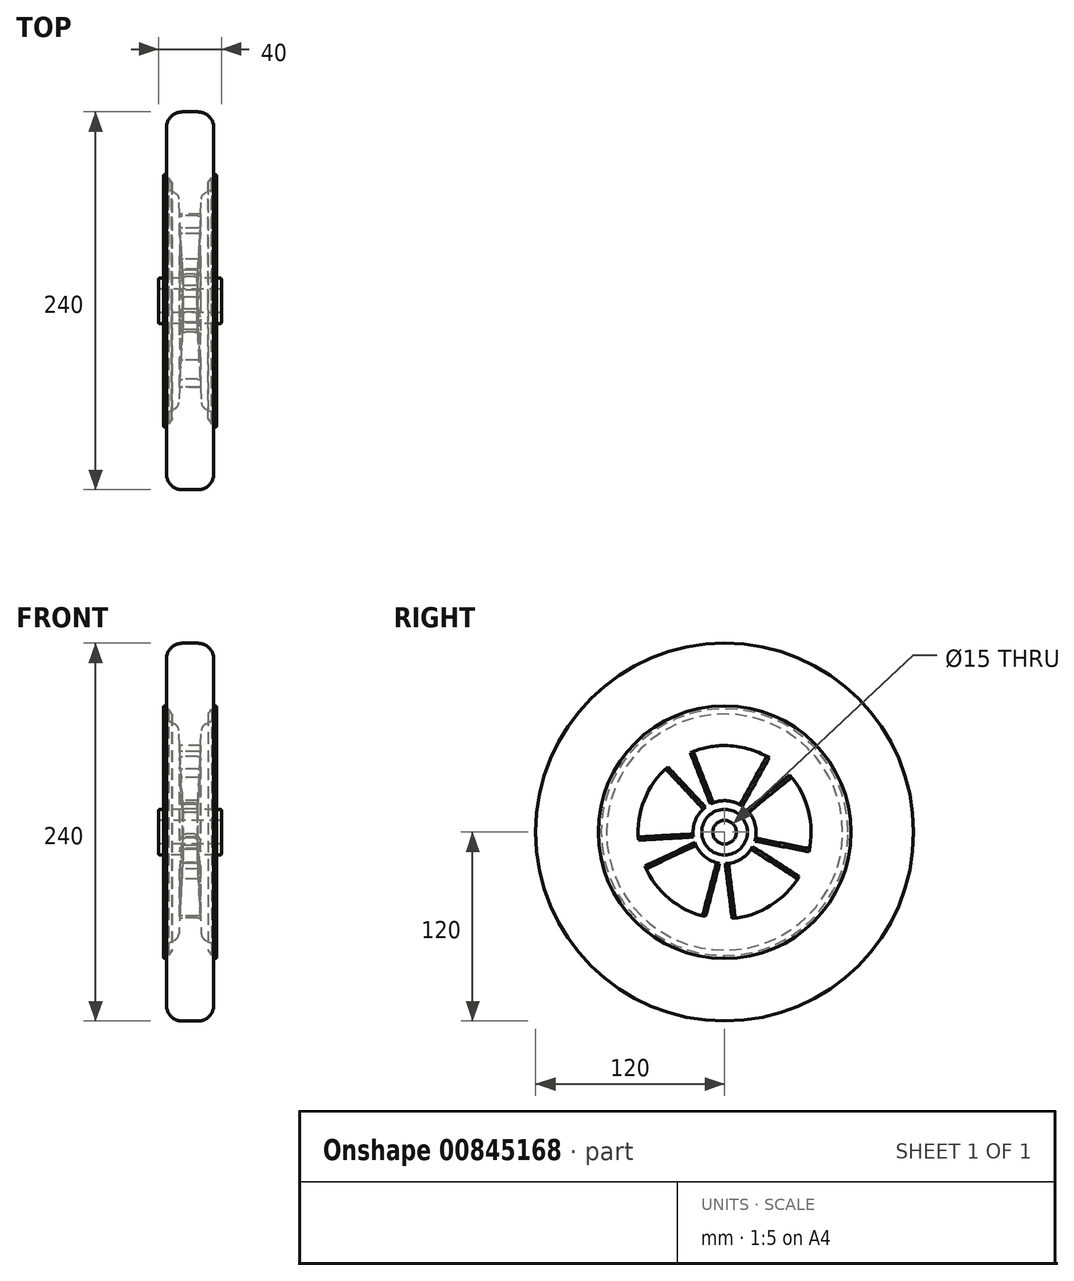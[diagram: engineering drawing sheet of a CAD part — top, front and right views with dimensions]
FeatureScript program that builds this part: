
annotation { "Feature Type Name" : "Feature", "Feature Type Description" : "" }
export const myFeature = defineFeature(function(context is Context, id is Id, definition is map)
    precondition{}
    {
        {
            var Q0;
            Q0=qCreatedBy(makeId("Top.planeOp"),FACE);
            var sketch = newSketch(context, id + "F0", { "sketchPlane" : qUnion([Q0])});
            skLineSegment(sketch, "E0", {"start": v(-229, 0) * mm, "end": v(229, 0) * mm});
            skLineSegment(sketch, "E1", {"start": v(0, 0) * mm, "end": v(0, 120) * mm, "construction": true});
            skLineSegment(sketch, "E2", {"start": v(0, 7.5) * mm, "end": v(-20, 7.5) * mm});
            skLineSegment(sketch, "E3", {"start": v(-20, 7.5) * mm, "end": v(-20, 14.5) * mm});
            skLineSegment(sketch, "E4", {"start": v(-20, 14.5) * mm, "end": v(-4.5, 14.5) * mm});
            skLineSegment(sketch, "E5", {"start": v(-4.5, 14.5) * mm, "end": v(-7.12, 64.5) * mm});
            skLineSegment(sketch, "E6", {"start": v(0, 75) * mm, "end": v(-11.6, 75) * mm});
            skLineSegment(sketch, "E7", {"start": v(-11.6, 75) * mm, "end": v(-14.88, 80.24) * mm});
            skLineSegment(sketch, "E8", {"start": v(-14.88, 80.24) * mm, "end": v(-15.88, 80.24) * mm});
            skLineSegment(sketch, "E9", {"start": v(-9.92, 68.72) * mm, "end": v(-13.12, 70.29) * mm});
            skLineSegment(sketch, "E10", {"start": v(-13.61, 70.82) * mm, "end": v(-16.8, 78.88) * mm});
            skPoint(sketch, "E11.visualSharp", {"position": v(-17.35, 80.24) * mm});
            skArc(sketch, "E11.filletArc", {"start": v(-15.88, 80.24) * mm, "mid": v(-16.7, 79.8) * mm, "end": v(-16.8, 78.88) * mm});
            skPoint(sketch, "E12.visualSharp", {"position": v(-13.47, 70.46) * mm});
            skArc(sketch, "E12.filletArc", {"start": v(-13.61, 70.82) * mm, "mid": v(-13.42, 70.5) * mm, "end": v(-13.12, 70.29) * mm});
            skPoint(sketch, "E13.visualSharp", {"position": v(-7.27, 67.43) * mm});
            skArc(sketch, "E13.filletArc", {"start": v(-7.12, 64.5) * mm, "mid": v(-7.94, 66.99) * mm, "end": v(-9.92, 68.72) * mm});
            skLineSegment(sketch, "E14", {"start": v(0, 120) * mm, "end": v(-5, 120) * mm});
            skLineSegment(sketch, "E15", {"start": v(-15, 110) * mm, "end": v(-15, 80.8) * mm});
            skLineSegment(sketch, "E16", {"start": v(-14.75, 79.97) * mm, "end": v(-11.5, 75) * mm});
            skLineSegment(sketch, "E17", {"start": v(-11.5, 75) * mm, "end": v(0, 75) * mm});
            skPoint(sketch, "E18.visualSharp", {"position": v(-15, 80.35) * mm});
            skArc(sketch, "E18.filletArc", {"start": v(-15, 80.8) * mm, "mid": v(-14.94, 80.36) * mm, "end": v(-14.75, 79.97) * mm});
            skPoint(sketch, "E19.visualSharp", {"position": v(-15, 120) * mm});
            skArc(sketch, "E19.filletArc", {"start": v(-5, 120) * mm, "mid": v(-12.07, 117.07) * mm, "end": v(-15, 110) * mm});
            skLineSegment(sketch, "E20.MirrorCS", {"start": v(0, 7.5) * mm, "end": v(20, 7.5) * mm});
            skLineSegment(sketch, "E21.MirrorCS", {"start": v(20, 7.5) * mm, "end": v(20, 14.5) * mm});
            skLineSegment(sketch, "E22.MirrorCS", {"start": v(20, 14.5) * mm, "end": v(4.5, 14.5) * mm});
            skLineSegment(sketch, "E23.MirrorCS", {"start": v(4.5, 14.5) * mm, "end": v(7.12, 64.5) * mm});
            skArc(sketch, "E24.MirrorCS", {"start": v(7.12, 64.5) * mm, "mid": v(7.94, 66.99) * mm, "end": v(9.92, 68.72) * mm});
            skLineSegment(sketch, "E25.MirrorCS", {"start": v(9.92, 68.72) * mm, "end": v(13.12, 70.29) * mm});
            skArc(sketch, "E26.MirrorCS", {"start": v(13.61, 70.82) * mm, "mid": v(13.42, 70.5) * mm, "end": v(13.12, 70.29) * mm});
            skLineSegment(sketch, "E27.MirrorCS", {"start": v(13.61, 70.82) * mm, "end": v(16.8, 78.88) * mm});
            skArc(sketch, "E28.MirrorCS", {"start": v(15.88, 80.24) * mm, "mid": v(16.7, 79.8) * mm, "end": v(16.8, 78.88) * mm});
            skLineSegment(sketch, "E29.MirrorCS", {"start": v(14.88, 80.24) * mm, "end": v(15.88, 80.24) * mm});
            skLineSegment(sketch, "E30.MirrorCS", {"start": v(11.6, 75) * mm, "end": v(14.88, 80.24) * mm});
            skLineSegment(sketch, "E31.MirrorCS", {"start": v(0, 75) * mm, "end": v(11.6, 75) * mm});
            skLineSegment(sketch, "E32.MirrorCS", {"start": v(11.5, 75) * mm, "end": v(0, 75) * mm});
            skLineSegment(sketch, "E33.MirrorCS", {"start": v(14.75, 79.97) * mm, "end": v(11.5, 75) * mm});
            skArc(sketch, "E34.MirrorCS", {"start": v(15, 80.8) * mm, "mid": v(14.94, 80.36) * mm, "end": v(14.75, 79.97) * mm});
            skLineSegment(sketch, "E35.MirrorCS", {"start": v(15, 110) * mm, "end": v(15, 80.8) * mm});
            skArc(sketch, "E36.MirrorCS", {"start": v(5, 120) * mm, "mid": v(12.07, 117.07) * mm, "end": v(15, 110) * mm});
            skLineSegment(sketch, "E37.MirrorCS", {"start": v(0, 120) * mm, "end": v(5, 120) * mm});
            skSolve(sketch);
        }
        {
            var Q0;
            {var subQ0=sQuery(id+"F0.wireOp",EDGE,"E8");var subQ1=sQuery(id+"F0.wireOp",EDGE,"E7");var subQ2=makeQuery(id+"F0.imprint","INTERSECT",VERTEX,{"derivedFrom":[subQ1,subQ0]});Q0=makeQuery(id+"F0.imprint","IMPRINT",FACE,{"disambiguationData":[TD([[makeQuery(id+"F0.imprint","IMPRINT",EDGE,{"disambiguationData":[TD([[subQ2,1.0]])],"derivedFrom":subQ1}),1.0]])]});}
            var Q1;
            {var subQ0=sQuery(id+"F0.wireOp",EDGE,"E30.MirrorCS");var subQ1=sQuery(id+"F0.wireOp",EDGE,"E29.MirrorCS");var subQ2=makeQuery(id+"F0.imprint","INTERSECT",VERTEX,{"derivedFrom":[subQ1,subQ0]});Q1=makeQuery(id+"F0.imprint","IMPRINT",FACE,{"disambiguationData":[TD([[makeQuery(id+"F0.imprint","IMPRINT",EDGE,{"disambiguationData":[TD([[subQ2,-1.0]])],"derivedFrom":subQ1}),-1.0]])]});}
            var Q2;
            Q2=makeQuery(id+"F0.imprint","IMPRINT",FACE,{"disambiguationData":[TD([[makeQuery(id+"F0.imprint","IMPRINT",EDGE,{"derivedFrom":sQuery(id+"F0.wireOp",EDGE,"E14")}),1.0]])]});
            var Q3;
            Q3=makeQuery(id+"F0.imprint","IMPRINT",FACE,{"disambiguationData":[TD([[makeQuery(id+"F0.imprint","IMPRINT",EDGE,{"derivedFrom":sQuery(id+"F0.wireOp",EDGE,"E2")}),-1.0]])]});
            var Q4;
            Q4=sQuery(id+"F0.wireOp",EDGE,"E0");
            revolve(context, id + "F1", {"surfaceOperationType" : NewSurfaceOperationType.NEW, "entities" : qUnion([Q0, Q1, Q2, Q3]), "axis" : qUnion([Q4]), "revolveType" : RevolveType.FULL});
        }
        {
            var Q0;
            Q0=makeQuery(id+"F1.opRevolve","SWEPT_FACE",FACE,{"disambiguationData":[OSD([sQuery(id+"F0.wireOp",EDGE,"E3")])]});
            var sketch = newSketch(context, id + "F2", { "sketchPlane" : qUnion([Q0])});
            skCircle(sketch, "E38", {"center": v(0, 0) * mm, "radius": 55 * mm});
            skCircle(sketch, "E39", {"center": v(0, 0) * mm, "radius": 20 * mm});
            skLineSegment(sketch, "E40", {"start": v(0, 0) * mm, "end": v(19.92, 51.27) * mm});
            skLineSegment(sketch, "E41", {"start": v(0, 0) * mm, "end": v(-26.64, 48.12) * mm});
            skLineSegment(sketch, "E42.1.0", {"start": v(0, 0) * mm, "end": v(-54, -10.47) * mm});
            skLineSegment(sketch, "E42.1.1", {"start": v(0, 0) * mm, "end": v(-42.6, 34.78) * mm});
            skLineSegment(sketch, "E42.2.0", {"start": v(0, 0) * mm, "end": v(-6.73, -54.59) * mm});
            skLineSegment(sketch, "E42.2.1", {"start": v(0, 0) * mm, "end": v(-46.25, -29.77) * mm});
            skLineSegment(sketch, "E42.3.0", {"start": v(0, 0) * mm, "end": v(49.84, -23.27) * mm});
            skLineSegment(sketch, "E42.3.1", {"start": v(0, 0) * mm, "end": v(14.02, -53.18) * mm});
            skLineSegment(sketch, "E42.4.0", {"start": v(0, 0) * mm, "end": v(37.53, 40.2) * mm});
            skLineSegment(sketch, "E42.4.1", {"start": v(0, 0) * mm, "end": v(54.91, -3.1) * mm});
            skSolve(sketch);
        }
        {
            var Q0;
            {var subQ0=sQuery(id+"F2.wireOp",EDGE,"E40");var subQ1=sQuery(id+"F2.wireOp",EDGE,"E38");var subQ2=makeQuery(id+"F2.imprint","INTERSECT",VERTEX,{"derivedFrom":[subQ1,subQ0]});Q0=makeQuery(id+"F2.imprint","IMPRINT",FACE,{"disambiguationData":[TD([[makeQuery(id+"F2.imprint","IMPRINT",EDGE,{"disambiguationData":[TD([[subQ2,-1.0]])],"derivedFrom":subQ1}),1.0]])]});}
            var Q1;
            {var subQ0=sQuery(id+"F2.wireOp",EDGE,"E42.4.0");var subQ1=sQuery(id+"F2.wireOp",EDGE,"E38");var subQ2=makeQuery(id+"F2.imprint","INTERSECT",VERTEX,{"derivedFrom":[subQ1,subQ0]});Q1=makeQuery(id+"F2.imprint","IMPRINT",FACE,{"disambiguationData":[TD([[makeQuery(id+"F2.imprint","IMPRINT",EDGE,{"disambiguationData":[TD([[subQ2,1.0]])],"derivedFrom":subQ1}),1.0]])]});}
            var Q2;
            {var subQ0=sQuery(id+"F2.wireOp",EDGE,"E42.3.0");var subQ1=sQuery(id+"F2.wireOp",EDGE,"E38");var subQ2=makeQuery(id+"F2.imprint","INTERSECT",VERTEX,{"derivedFrom":[subQ1,subQ0]});Q2=makeQuery(id+"F2.imprint","IMPRINT",FACE,{"disambiguationData":[TD([[makeQuery(id+"F2.imprint","IMPRINT",EDGE,{"disambiguationData":[TD([[subQ2,1.0]])],"derivedFrom":subQ1}),1.0]])]});}
            var Q3;
            {var subQ0=sQuery(id+"F2.wireOp",EDGE,"E42.2.0");var subQ1=sQuery(id+"F2.wireOp",EDGE,"E38");var subQ2=makeQuery(id+"F2.imprint","INTERSECT",VERTEX,{"derivedFrom":[subQ1,subQ0]});Q3=makeQuery(id+"F2.imprint","IMPRINT",FACE,{"disambiguationData":[TD([[makeQuery(id+"F2.imprint","IMPRINT",EDGE,{"disambiguationData":[TD([[subQ2,1.0]])],"derivedFrom":subQ1}),1.0]])]});}
            var Q4;
            {var subQ0=sQuery(id+"F2.wireOp",EDGE,"E42.1.0");var subQ1=sQuery(id+"F2.wireOp",EDGE,"E38");var subQ2=makeQuery(id+"F2.imprint","INTERSECT",VERTEX,{"derivedFrom":[subQ1,subQ0]});Q4=makeQuery(id+"F2.imprint","IMPRINT",FACE,{"disambiguationData":[TD([[makeQuery(id+"F2.imprint","IMPRINT",EDGE,{"disambiguationData":[TD([[subQ2,1.0]])],"derivedFrom":subQ1}),1.0]])]});}
            extrude(context, id + "F3", {"entities" : qUnion([Q0, Q1, Q2, Q3, Q4]), "operationType" : NewBodyOperationType.REMOVE, "oppositeDirection" : true, "depth" : 50 * mm, "offsetDistance" : 25 * mm});
        }
        {
            var Q0;
            Q0=makeQuery(id+"F3.boolean.opBoolean","INTERSECT",EDGE,{"derivedFrom":[makeQuery(id+"F1.opRevolve","SWEPT_FACE",FACE,{"disambiguationData":[OSD([sQuery(id+"F0.wireOp",EDGE,"E5")])]}),makeQuery(id+"F3.opExtrude","SWEPT_FACE",FACE,{"disambiguationData":[OSD([sQuery(id+"F2.wireOp",EDGE,"E42.1.0")])]})]});
            var Q1;
            Q1=makeQuery(id+"F3.boolean.opBoolean","INTERSECT",EDGE,{"derivedFrom":[makeQuery(id+"F1.opRevolve","SWEPT_FACE",FACE,{"disambiguationData":[OSD([sQuery(id+"F0.wireOp",EDGE,"E23.MirrorCS")])]}),makeQuery(id+"F3.opExtrude","SWEPT_FACE",FACE,{"disambiguationData":[OSD([sQuery(id+"F2.wireOp",EDGE,"E42.1.0")])]})]});
            var Q2;
            Q2=makeQuery(id+"F3.boolean.opBoolean","INTERSECT",EDGE,{"derivedFrom":[makeQuery(id+"F1.opRevolve","SWEPT_FACE",FACE,{"disambiguationData":[OSD([sQuery(id+"F0.wireOp",EDGE,"E5")])]}),makeQuery(id+"F3.opExtrude","SWEPT_FACE",FACE,{"disambiguationData":[OSD([sQuery(id+"F2.wireOp",EDGE,"E42.1.1")])]})]});
            var Q3;
            Q3=makeQuery(id+"F3.boolean.opBoolean","INTERSECT",EDGE,{"derivedFrom":[makeQuery(id+"F1.opRevolve","SWEPT_FACE",FACE,{"disambiguationData":[OSD([sQuery(id+"F0.wireOp",EDGE,"E5")])]}),makeQuery(id+"F3.opExtrude","SWEPT_FACE",FACE,{"disambiguationData":[OSD([sQuery(id+"F2.wireOp",EDGE,"E41")])]})]});
            var Q4;
            Q4=makeQuery(id+"F3.boolean.opBoolean","INTERSECT",EDGE,{"derivedFrom":[makeQuery(id+"F1.opRevolve","SWEPT_FACE",FACE,{"disambiguationData":[OSD([sQuery(id+"F0.wireOp",EDGE,"E23.MirrorCS")])]}),makeQuery(id+"F3.opExtrude","SWEPT_FACE",FACE,{"disambiguationData":[OSD([sQuery(id+"F2.wireOp",EDGE,"E41")])]})]});
            var Q5;
            Q5=makeQuery(id+"F3.boolean.opBoolean","INTERSECT",EDGE,{"derivedFrom":[makeQuery(id+"F1.opRevolve","SWEPT_FACE",FACE,{"disambiguationData":[OSD([sQuery(id+"F0.wireOp",EDGE,"E5")])]}),makeQuery(id+"F3.opExtrude","SWEPT_FACE",FACE,{"disambiguationData":[OSD([sQuery(id+"F2.wireOp",EDGE,"E40")])]})]});
            var Q6;
            Q6=makeQuery(id+"F3.boolean.opBoolean","INTERSECT",EDGE,{"derivedFrom":[makeQuery(id+"F1.opRevolve","SWEPT_FACE",FACE,{"disambiguationData":[OSD([sQuery(id+"F0.wireOp",EDGE,"E5")])]}),makeQuery(id+"F3.opExtrude","SWEPT_FACE",FACE,{"disambiguationData":[OSD([sQuery(id+"F2.wireOp",EDGE,"E42.4.0")])]})]});
            var Q7;
            Q7=makeQuery(id+"F3.boolean.opBoolean","INTERSECT",EDGE,{"derivedFrom":[makeQuery(id+"F1.opRevolve","SWEPT_FACE",FACE,{"disambiguationData":[OSD([sQuery(id+"F0.wireOp",EDGE,"E5")])]}),makeQuery(id+"F3.opExtrude","SWEPT_FACE",FACE,{"disambiguationData":[OSD([sQuery(id+"F2.wireOp",EDGE,"E42.4.1")])]})]});
            var Q8;
            Q8=makeQuery(id+"F3.boolean.opBoolean","INTERSECT",EDGE,{"derivedFrom":[makeQuery(id+"F1.opRevolve","SWEPT_FACE",FACE,{"disambiguationData":[OSD([sQuery(id+"F0.wireOp",EDGE,"E23.MirrorCS")])]}),makeQuery(id+"F3.opExtrude","SWEPT_FACE",FACE,{"disambiguationData":[OSD([sQuery(id+"F2.wireOp",EDGE,"E42.4.1")])]})]});
            var Q9;
            Q9=makeQuery(id+"F3.boolean.opBoolean","INTERSECT",EDGE,{"derivedFrom":[makeQuery(id+"F1.opRevolve","SWEPT_FACE",FACE,{"disambiguationData":[OSD([sQuery(id+"F0.wireOp",EDGE,"E5")])]}),makeQuery(id+"F3.opExtrude","SWEPT_FACE",FACE,{"disambiguationData":[OSD([sQuery(id+"F2.wireOp",EDGE,"E42.3.0")])]})]});
            var Q10;
            Q10=makeQuery(id+"F3.boolean.opBoolean","INTERSECT",EDGE,{"derivedFrom":[makeQuery(id+"F1.opRevolve","SWEPT_FACE",FACE,{"disambiguationData":[OSD([sQuery(id+"F0.wireOp",EDGE,"E5")])]}),makeQuery(id+"F3.opExtrude","SWEPT_FACE",FACE,{"disambiguationData":[OSD([sQuery(id+"F2.wireOp",EDGE,"E42.3.1")])]})]});
            var Q11;
            Q11=makeQuery(id+"F3.boolean.opBoolean","INTERSECT",EDGE,{"derivedFrom":[makeQuery(id+"F1.opRevolve","SWEPT_FACE",FACE,{"disambiguationData":[OSD([sQuery(id+"F0.wireOp",EDGE,"E23.MirrorCS")])]}),makeQuery(id+"F3.opExtrude","SWEPT_FACE",FACE,{"disambiguationData":[OSD([sQuery(id+"F2.wireOp",EDGE,"E42.3.1")])]})]});
            var Q12;
            Q12=makeQuery(id+"F3.boolean.opBoolean","INTERSECT",EDGE,{"derivedFrom":[makeQuery(id+"F1.opRevolve","SWEPT_FACE",FACE,{"disambiguationData":[OSD([sQuery(id+"F0.wireOp",EDGE,"E5")])]}),makeQuery(id+"F3.opExtrude","SWEPT_FACE",FACE,{"disambiguationData":[OSD([sQuery(id+"F2.wireOp",EDGE,"E42.2.0")])]})]});
            var Q13;
            Q13=makeQuery(id+"F3.boolean.opBoolean","INTERSECT",EDGE,{"derivedFrom":[makeQuery(id+"F1.opRevolve","SWEPT_FACE",FACE,{"disambiguationData":[OSD([sQuery(id+"F0.wireOp",EDGE,"E5")])]}),makeQuery(id+"F3.opExtrude","SWEPT_FACE",FACE,{"disambiguationData":[OSD([sQuery(id+"F2.wireOp",EDGE,"E42.2.1")])]})]});
            var Q14;
            Q14=makeQuery(id+"F3.boolean.opBoolean","INTERSECT",EDGE,{"derivedFrom":[makeQuery(id+"F1.opRevolve","SWEPT_FACE",FACE,{"disambiguationData":[OSD([sQuery(id+"F0.wireOp",EDGE,"E23.MirrorCS")])]}),makeQuery(id+"F3.opExtrude","SWEPT_FACE",FACE,{"disambiguationData":[OSD([sQuery(id+"F2.wireOp",EDGE,"E42.1.1")])]})]});
            var Q15;
            Q15=makeQuery(id+"F3.boolean.opBoolean","INTERSECT",EDGE,{"derivedFrom":[makeQuery(id+"F1.opRevolve","SWEPT_FACE",FACE,{"disambiguationData":[OSD([sQuery(id+"F0.wireOp",EDGE,"E23.MirrorCS")])]}),makeQuery(id+"F3.opExtrude","SWEPT_FACE",FACE,{"disambiguationData":[OSD([sQuery(id+"F2.wireOp",EDGE,"E40")])]})]});
            var Q16;
            Q16=makeQuery(id+"F3.boolean.opBoolean","INTERSECT",EDGE,{"derivedFrom":[makeQuery(id+"F1.opRevolve","SWEPT_FACE",FACE,{"disambiguationData":[OSD([sQuery(id+"F0.wireOp",EDGE,"E23.MirrorCS")])]}),makeQuery(id+"F3.opExtrude","SWEPT_FACE",FACE,{"disambiguationData":[OSD([sQuery(id+"F2.wireOp",EDGE,"E42.3.0")])]})]});
            var Q17;
            Q17=makeQuery(id+"F3.boolean.opBoolean","INTERSECT",EDGE,{"derivedFrom":[makeQuery(id+"F1.opRevolve","SWEPT_FACE",FACE,{"disambiguationData":[OSD([sQuery(id+"F0.wireOp",EDGE,"E23.MirrorCS")])]}),makeQuery(id+"F3.opExtrude","SWEPT_FACE",FACE,{"disambiguationData":[OSD([sQuery(id+"F2.wireOp",EDGE,"E42.2.0")])]})]});
            var Q18;
            Q18=makeQuery(id+"F3.boolean.opBoolean","INTERSECT",EDGE,{"derivedFrom":[makeQuery(id+"F1.opRevolve","SWEPT_FACE",FACE,{"disambiguationData":[OSD([sQuery(id+"F0.wireOp",EDGE,"E23.MirrorCS")])]}),makeQuery(id+"F3.opExtrude","SWEPT_FACE",FACE,{"disambiguationData":[OSD([sQuery(id+"F2.wireOp",EDGE,"E42.2.1")])]})]});
            var Q19;
            Q19=makeQuery(id+"F3.boolean.opBoolean","INTERSECT",EDGE,{"derivedFrom":[makeQuery(id+"F1.opRevolve","SWEPT_FACE",FACE,{"disambiguationData":[OSD([sQuery(id+"F0.wireOp",EDGE,"E23.MirrorCS")])]}),makeQuery(id+"F3.opExtrude","SWEPT_FACE",FACE,{"disambiguationData":[OSD([sQuery(id+"F2.wireOp",EDGE,"E42.4.0")])]})]});
            fillet(context, id + "F4", {"entities" : qUnion([Q0, Q1, Q2, Q3, Q4, Q5, Q6, Q7, Q8, Q9, Q10, Q11, Q12, Q13, Q14, Q15, Q16, Q17, Q18, Q19]), "radius" : 2 * mm, "tangentPropagation" : true, "allowEdgeOverflow" : false});
        }
        {
            var Q0;
            Q0=makeQuery(id+"F1.opRevolve","SWEPT_EDGE",EDGE,{"disambiguationData":[OSD([sQuery(id+"F0.wireOp",EDGE,"E3"),sQuery(id+"F0.wireOp",EDGE,"E4")])]});
            var Q1;
            Q1=makeQuery(id+"F1.opRevolve","SWEPT_EDGE",EDGE,{"disambiguationData":[OSD([sQuery(id+"F0.wireOp",EDGE,"E21.MirrorCS"),sQuery(id+"F0.wireOp",EDGE,"E22.MirrorCS")])]});
            fillet(context, id + "F5", {"entities" : qUnion([Q0, Q1]), "radius" : 1 * mm, "tangentPropagation" : true, "allowEdgeOverflow" : false});
        }
    });
